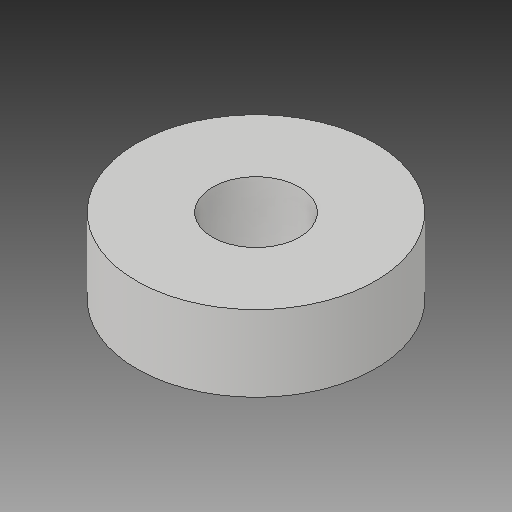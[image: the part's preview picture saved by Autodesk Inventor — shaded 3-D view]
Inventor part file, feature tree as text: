
AUTODESK INVENTOR PART (.ipt)
format: ipt  version: 2017 (Build 210142000, 142)  size: 100,864 bytes
history: native  units: mm
features: extrude x1, sketch x1
ambient origin geometry x8: Origin, YZ Plane, XZ Plane, XY Plane, X Axis, Y Axis, Z Axis, Center Point
bodies: Body1 (feature_tree)
feature tree (2):
  extrude  "Extrusion1"  Depth=7.0mm
  sketch  "Sketch2"  dims[d21=8.0mm d22=22.0mm d23=7.0mm d24=0.0mm]
